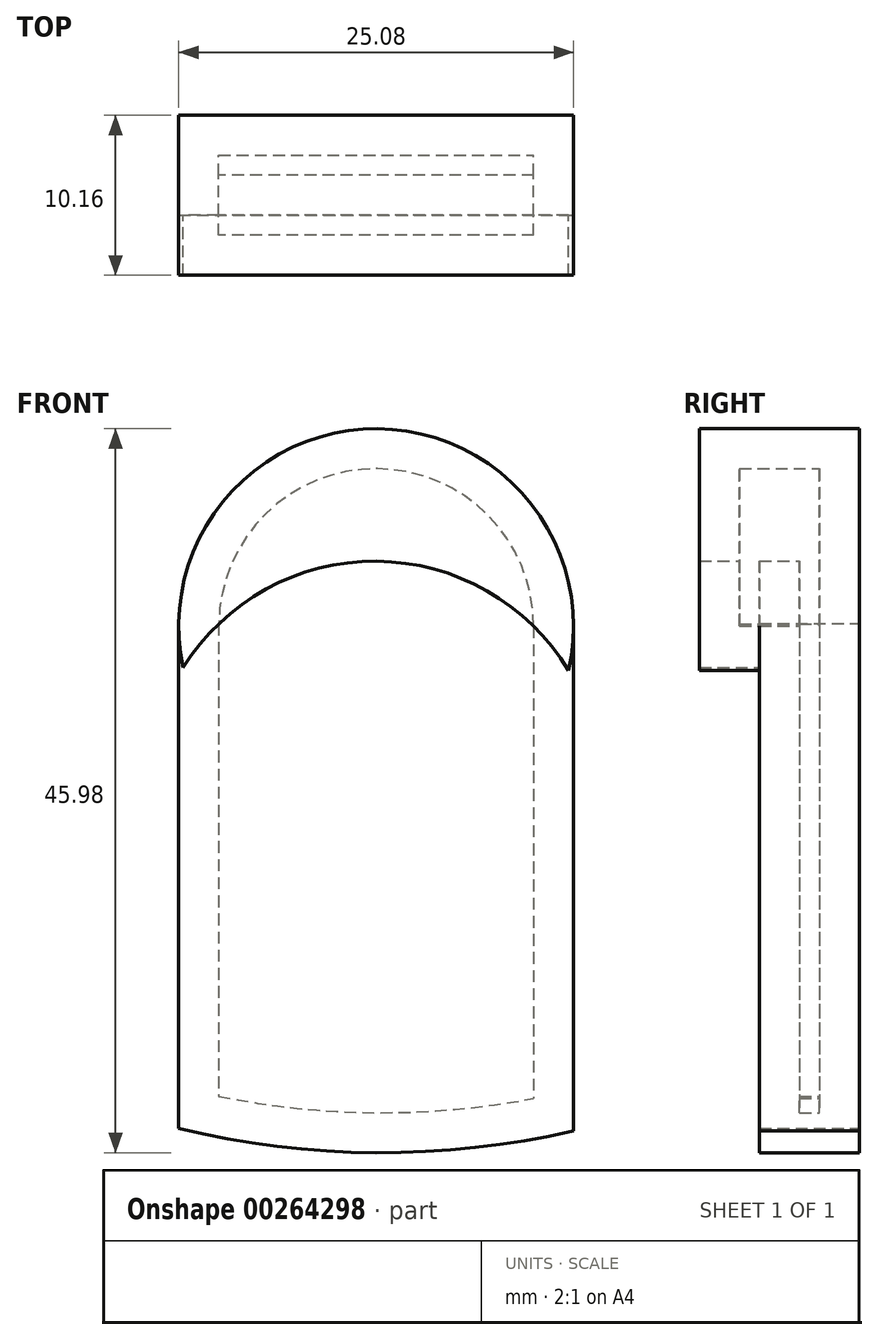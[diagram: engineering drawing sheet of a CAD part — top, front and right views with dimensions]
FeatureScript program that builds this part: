
annotation { "Feature Type Name" : "Feature", "Feature Type Description" : "" }
export const myFeature = defineFeature(function(context is Context, id is Id, definition is map)
    precondition{}
    {
        {
            var Q0;
            Q0=qCreatedBy(makeId("Front.planeOp"),FACE);
            var sketch = newSketch(context, id + "F0", { "sketchPlane" : qUnion([Q0])});
            skLineSegment(sketch, "E0", {"start": v(-20, 0.15) * mm, "end": v(-20, -29.85) * mm});
            skLineSegment(sketch, "E1", {"start": v(0, 0) * mm, "end": v(0, -30) * mm});
            skArc(sketch, "E2", {"start": v(-20, -29.85) * mm, "mid": v(-10, -30.9) * mm, "end": v(0, -30) * mm});
            skArc(sketch, "E3", {"start": v(0, 0) * mm, "mid": v(-9.93, 10) * mm, "end": v(-20, 0.15) * mm});
            skSolve(sketch);
        }
        {
            var Q0;
            Q0=makeQuery(id+"F0.imprint","IMPRINT",FACE,{"disambiguationData":[TD([[makeQuery(id+"F0.imprint","IMPRINT",EDGE,{"derivedFrom":sQuery(id+"F0.wireOp",EDGE,"E0")}),1.0]])]});
            extrude(context, id + "F1", {"entities" : qUnion([Q0]), "depth" : 1.27 * mm});
        }
        {
            var Q0;
            Q0=makeQuery(id+"F1.opExtrude","CAP_FACE",FACE,{"disambiguationData":[OSD([sQuery(id+"F0.wireOp",EDGE,"E0"),sQuery(id+"F0.wireOp",EDGE,"E1"),sQuery(id+"F0.wireOp",EDGE,"E2"),sQuery(id+"F0.wireOp",EDGE,"E3")])],"isStart":false});
            var sketch = newSketch(context, id + "F2", { "sketchPlane" : qUnion([Q0])});
            skArc(sketch, "E4", {"start": v(0, 0) * mm, "mid": v(-9.97, 4.13) * mm, "end": v(-20, 0.15) * mm});
            skSolve(sketch);
        }
        {
            var Q0;
            Q0=makeQuery(id+"F2.imprint","IMPRINT",FACE,{"disambiguationData":[TD([[makeQuery(id+"F2.imprint","IMPRINT",EDGE,{"derivedFrom":sQuery(id+"F2.wireOp",EDGE,"E4")}),-1.0]])]});
            extrude(context, id + "F3", {"entities" : qUnion([Q0]), "operationType" : NewBodyOperationType.ADD, "depth" : 3.8 * mm});
        }
        {
            var Q0;
            Q0=makeQuery(id+"F3.opExtrude","SWEPT_FACE",FACE,{"disambiguationData":[OSD([sQuery(id+"F2.wireOp",EDGE,"E4")])]});
            shell(context, id + "F4", {"entities" : qUnion([Q0]), "thickness" : 2.54 * mm, "oppositeDirection" : true});
        }
    });
